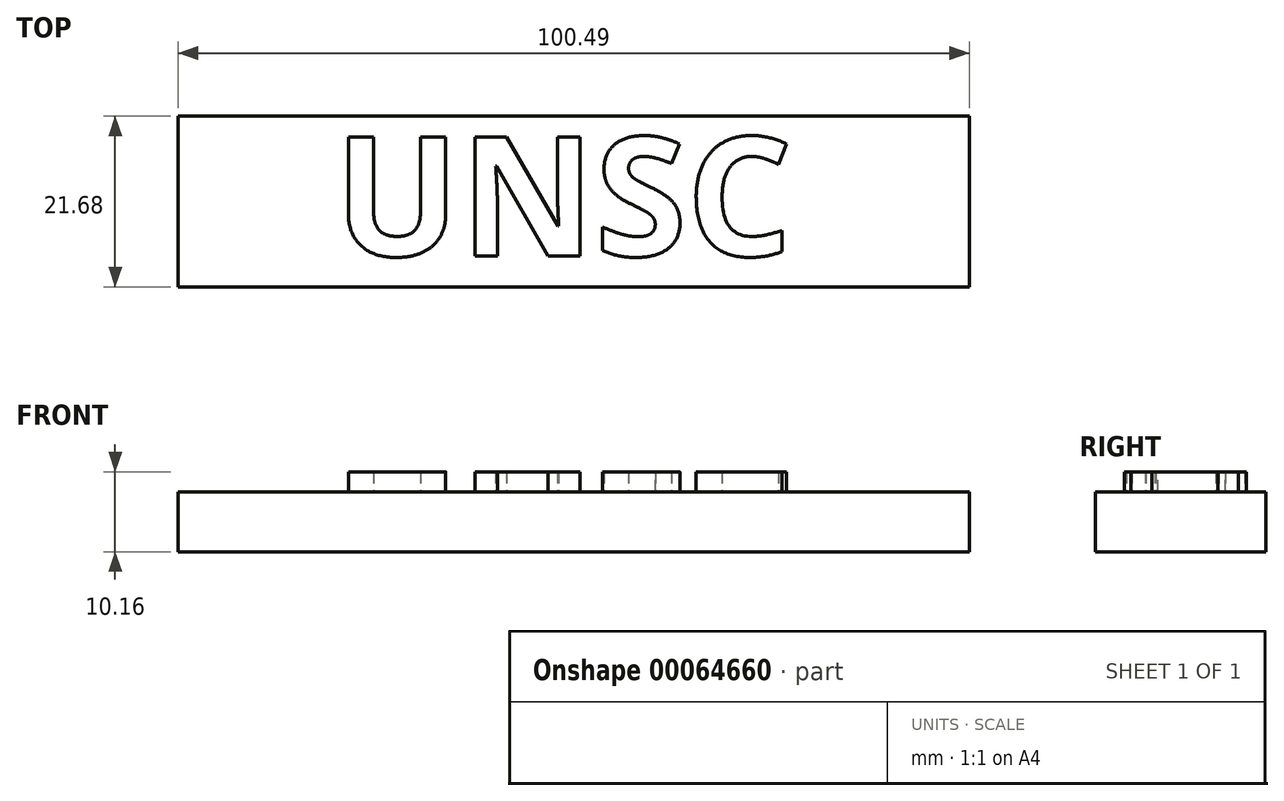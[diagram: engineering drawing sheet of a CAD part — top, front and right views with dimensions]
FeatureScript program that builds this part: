
annotation { "Feature Type Name" : "Feature", "Feature Type Description" : "" }
export const myFeature = defineFeature(function(context is Context, id is Id, definition is map)
    precondition{}
    {
        {
            var Q0;
            Q0=qCreatedBy(makeId("Top.planeOp"),FACE);
            var sketch = newSketch(context, id + "F0", { "sketchPlane" : qUnion([Q0])});
            skLineSegment(sketch, "E0.bottom", {"start": v(-46.35, 21.68) * mm, "end": v(54.14, 21.68) * mm});
            skLineSegment(sketch, "E0.top", {"start": v(-46.35, 0) * mm, "end": v(54.14, 0) * mm});
            skLineSegment(sketch, "E0.left", {"start": v(-46.35, 21.68) * mm, "end": v(-46.35, 0) * mm});
            skLineSegment(sketch, "E0.right", {"start": v(54.14, 21.68) * mm, "end": v(54.14, 0) * mm});
            skSolve(sketch);
        }
        {
            var Q0;
            Q0=makeQuery(id+"F0.imprint","IMPRINT",FACE,{"disambiguationData":[TD([[makeQuery(id+"F0.imprint","IMPRINT",EDGE,{"derivedFrom":sQuery(id+"F0.wireOp",EDGE,"E0.bottom")}),-1.0]])]});
            extrude(context, id + "F1", {"entities" : qUnion([Q0]), "depth" : 7.62 * mm});
        }
        {
            var Q0;
            Q0=makeQuery(id+"F1.opExtrude","CAP_FACE",FACE,{"disambiguationData":[OSD([sQuery(id+"F0.wireOp",EDGE,"E0.bottom"),sQuery(id+"F0.wireOp",EDGE,"E0.top"),sQuery(id+"F0.wireOp",EDGE,"E0.left"),sQuery(id+"F0.wireOp",EDGE,"E0.right")])],"isStart":false});
            var sketch = newSketch(context, id + "F2", { "sketchPlane" : qUnion([Q0])});
            skPoint(sketch, "E1", {"position": v(-46.35, 21.68) * mm});
            skPoint(sketch, "E2", {"position": v(54.14, 21.68) * mm});
            skText(sketch, "E3", { "text": "UNSC", "fontName": "OpenSans-Bold.ttf"});
            const initialGuessF2  = {"E3": [-0.02653, 0.00393, 1, 0, 0.0152]};
            skSetInitialGuess(sketch, initialGuessF2);
            skSolve(sketch);
        }
        {
            var Q0;
            Q0 = qSketchRegion(id + "F2", true);
            extrude(context, id + "F3", {"entities" : qUnion([Q0]), "operationType" : NewBodyOperationType.ADD, "depth" : 2.54 * mm});
        }
    });
